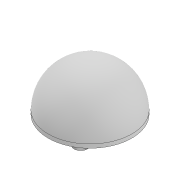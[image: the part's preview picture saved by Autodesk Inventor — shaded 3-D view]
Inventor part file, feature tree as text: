
AUTODESK INVENTOR PART (.ipt)
format: ipt  version: 2020 (Build 240168000, 168)  size: 194,560 bytes
history: native  units: mm
features: sketch x3, extrude x2, revolve x1, shell x1
ambient origin geometry x8: Origin, YZ Plane, XZ Plane, XY Plane, X Axis, Y Axis, Z Axis, Center Point
bodies: Solid1 (feature_tree)
feature tree (7):
  extrude  "Extrusion1"  Depth=30.0mm
  revolve  "Revolution1"  [1 undecoded]
  shell  "Shell1"  Thickness=3.1mm
  extrude  "Extrusion2"  Depth=2.0mm
  sketch  "Sketch1"  dims[d0=20.0mm d1=30.0mm]
  sketch  "Sketch2"  dims[d2=3.1mm d3=3.1mm d4=3.1mm]
  sketch  "Sketch4"  dims[d5=3.1mm d6=45.0mm d7=2.0mm d8=0.0mm d9=180.0deg d10=2.0mm d11=2.0mm d12=0.0mm]
note: 1 required parameter value undecoded (feature->parameter linkage not recoverable at this tier; creation-order binding heuristic only, values carry confidence <= 0.55)
